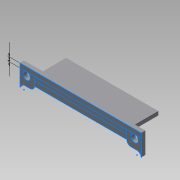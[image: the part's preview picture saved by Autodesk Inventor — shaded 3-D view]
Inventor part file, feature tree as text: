
AUTODESK INVENTOR PART (.ipt)
format: ipt  version: 2015 SP1 (Build 190203100, 203)  size: 109,568 bytes
history: native  units: mm
features: extrude x4, sketch x1
ambient origin geometry x8: Origin, YZ Plane, XZ Plane, XY Plane, X Axis, Y Axis, Z Axis, Center Point
bodies: Solid1 (feature_tree)
feature tree (5):
  sketch  "Sketch1"  dims[d0=2.0mm d1=0.0mm d2=15.0mm d3=0.0mm d4=1.0mm d5=0.0mm d6=2.0mm d7=2.0mm d8=0.0mm]
  extrude  "Extrusion1"  Depth=15.0mm TaperAngle=0.0deg
  extrude  "Extrusion2"  Depth=1.0mm TaperAngle=0.0deg
  extrude  "Extrusion3"  Depth=2.0mm
  extrude  "Extrusion4"  Depth=2.0mm TaperAngle=0.0deg
